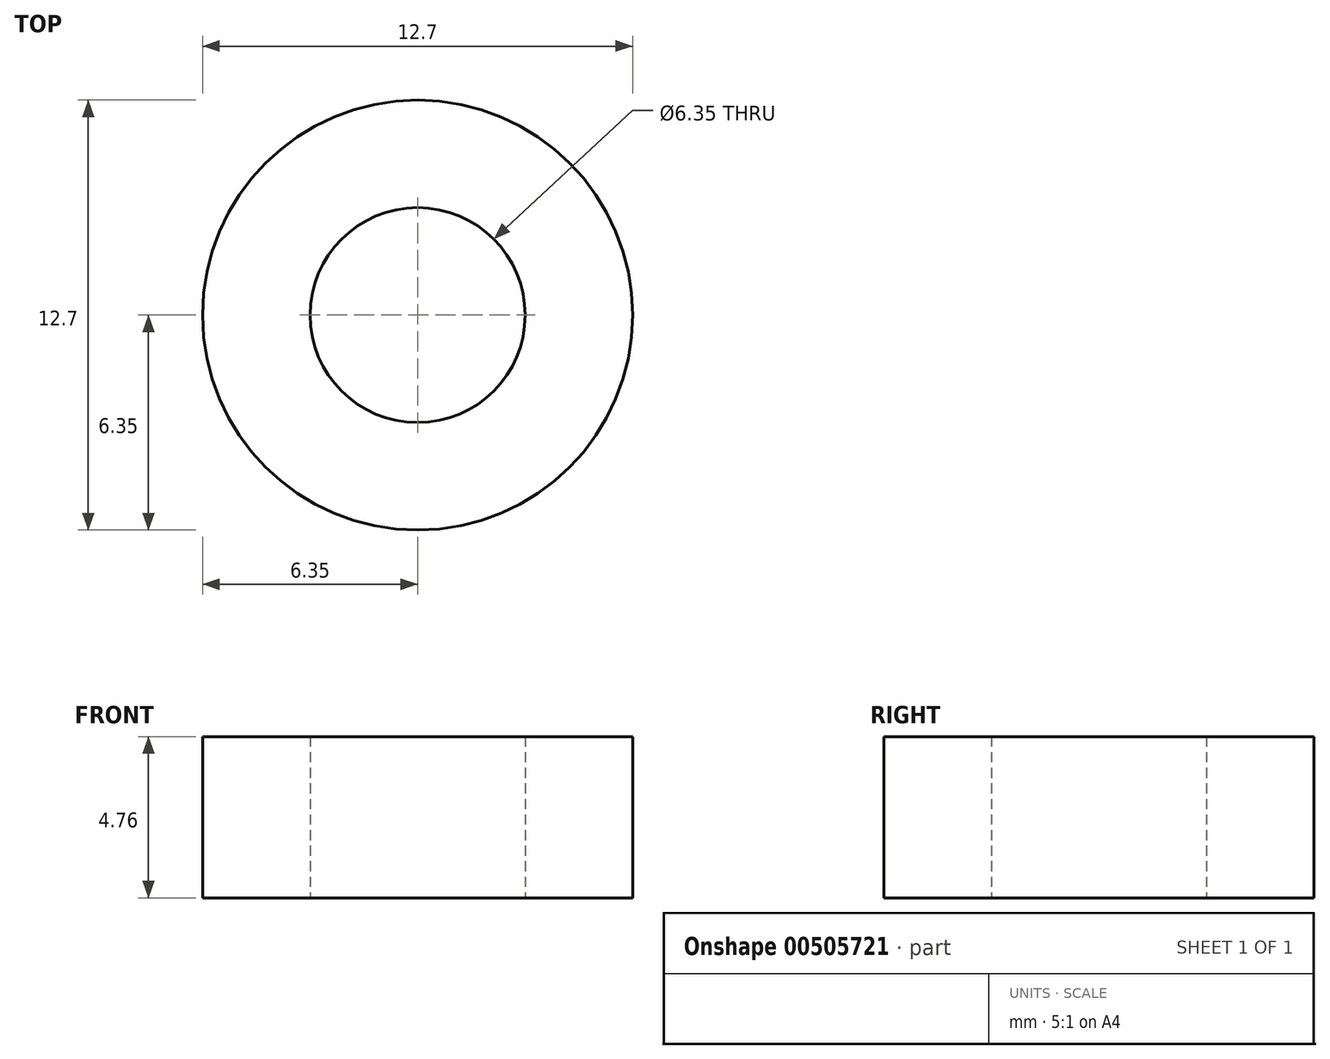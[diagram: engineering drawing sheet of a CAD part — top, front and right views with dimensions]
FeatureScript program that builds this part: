
annotation { "Feature Type Name" : "Feature", "Feature Type Description" : "" }
export const myFeature = defineFeature(function(context is Context, id is Id, definition is map)
    precondition{}
    {
        {
            var Q0;
            Q0=qCreatedBy(makeId("Right.planeOp"),FACE);
            var sketch = newSketch(context, id + "F0", { "sketchPlane" : qUnion([Q0])});
            skLineSegment(sketch, "E0", {"start": v(0, 0) * mm, "end": v(0, 11.79) * mm, "construction": true});
            skLineSegment(sketch, "E1.bottom", {"start": v(-6.35, 4.76) * mm, "end": v(-3.18, 4.76) * mm});
            skLineSegment(sketch, "E1.top", {"start": v(-6.35, 0) * mm, "end": v(-3.18, 0) * mm});
            skLineSegment(sketch, "E1.left", {"start": v(-6.35, 4.76) * mm, "end": v(-6.35, 0) * mm});
            skLineSegment(sketch, "E1.right", {"start": v(-3.18, 4.76) * mm, "end": v(-3.18, 0) * mm});
            skSolve(sketch);
        }
        {
            var Q0;
            Q0 = qSketchRegion(id + "F0", true);
            var Q1;
            Q1=sQuery(id+"F0.wireOp",EDGE,"E0");
            revolve(context, id + "F1", {"entities" : qUnion([Q0]), "axis" : qUnion([Q1]), "revolveType" : RevolveType.FULL});
        }
    });
